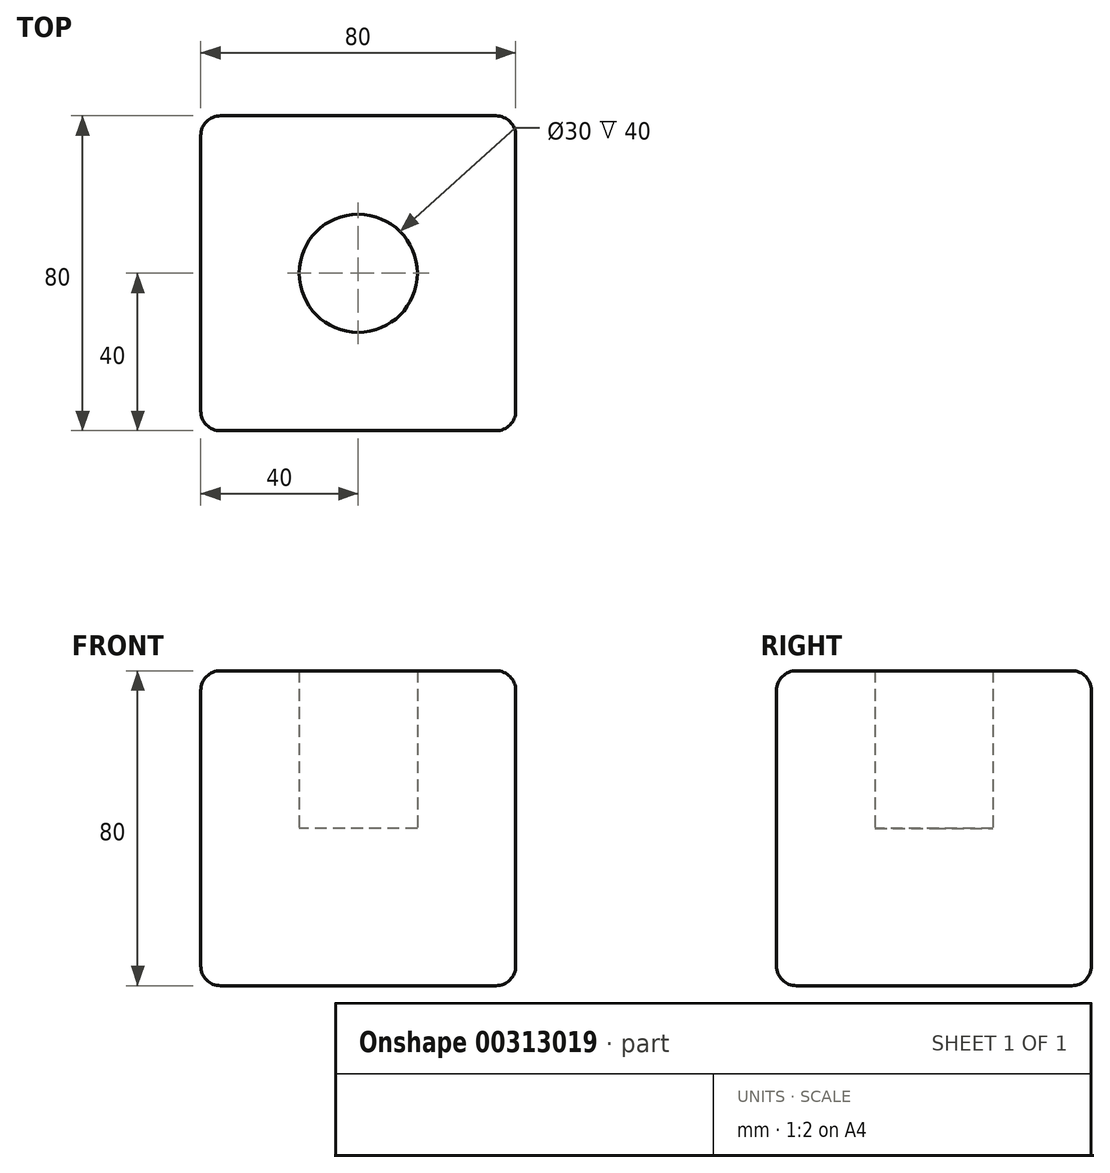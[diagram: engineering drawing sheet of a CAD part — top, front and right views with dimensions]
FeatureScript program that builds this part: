
annotation { "Feature Type Name" : "Feature", "Feature Type Description" : "" }
export const myFeature = defineFeature(function(context is Context, id is Id, definition is map)
    precondition{}
    {
        {
            var Q0;
            Q0=qCreatedBy(makeId("Top.planeOp"),FACE);
            var sketch = newSketch(context, id + "F0", { "sketchPlane" : qUnion([Q0])});
            skLineSegment(sketch, "E0.bottom", {"start": v(-40, 40) * mm, "end": v(40, 40) * mm});
            skLineSegment(sketch, "E0.top", {"start": v(-40, -40) * mm, "end": v(40, -40) * mm});
            skLineSegment(sketch, "E0.left", {"start": v(-40, 40) * mm, "end": v(-40, -40) * mm});
            skLineSegment(sketch, "E0.right", {"start": v(40, 40) * mm, "end": v(40, -40) * mm});
            skPoint(sketch, "E0.middle", {"position": v(0, 0) * mm});
            skSolve(sketch);
        }
        {
            var Q0;
            Q0=makeQuery(id+"F0.imprint","IMPRINT",FACE,{"disambiguationData":[TD([[makeQuery(id+"F0.imprint","IMPRINT",EDGE,{"derivedFrom":sQuery(id+"F0.wireOp",EDGE,"E0.bottom")}),-1.0]])]});
            extrude(context, id + "F1", {"entities" : qUnion([Q0]), "endBound" : BoundingType.SYMMETRIC, "depth" : 80 * mm});
        }
        {
            var Q0;
            Q0=makeQuery(id+"F1.opExtrude","CAP_EDGE",EDGE,{"disambiguationData":[OSD([sQuery(id+"F0.wireOp",EDGE,"E0.bottom")])],"isStart":false});
            var Q1;
            Q1=makeQuery(id+"F1.opExtrude","CAP_EDGE",EDGE,{"disambiguationData":[OSD([sQuery(id+"F0.wireOp",EDGE,"E0.left")])],"isStart":false});
            var Q2;
            Q2=makeQuery(id+"F1.opExtrude","CAP_EDGE",EDGE,{"disambiguationData":[OSD([sQuery(id+"F0.wireOp",EDGE,"E0.top")])],"isStart":false});
            var Q3;
            Q3=makeQuery(id+"F1.opExtrude","CAP_EDGE",EDGE,{"disambiguationData":[OSD([sQuery(id+"F0.wireOp",EDGE,"E0.right")])],"isStart":false});
            var Q4;
            Q4=makeQuery(id+"F1.opExtrude","SWEPT_EDGE",EDGE,{"disambiguationData":[OSD([sQuery(id+"F0.wireOp",EDGE,"E0.top"),sQuery(id+"F0.wireOp",EDGE,"E0.right")])]});
            var Q5;
            Q5=makeQuery(id+"F1.opExtrude","SWEPT_EDGE",EDGE,{"disambiguationData":[OSD([sQuery(id+"F0.wireOp",EDGE,"E0.bottom"),sQuery(id+"F0.wireOp",EDGE,"E0.right")])]});
            var Q6;
            Q6=makeQuery(id+"F1.opExtrude","CAP_EDGE",EDGE,{"disambiguationData":[OSD([sQuery(id+"F0.wireOp",EDGE,"E0.right")])],"isStart":true});
            var Q7;
            Q7=makeQuery(id+"F1.opExtrude","CAP_EDGE",EDGE,{"disambiguationData":[OSD([sQuery(id+"F0.wireOp",EDGE,"E0.top")])],"isStart":true});
            var Q8;
            Q8=makeQuery(id+"F1.opExtrude","SWEPT_EDGE",EDGE,{"disambiguationData":[OSD([sQuery(id+"F0.wireOp",EDGE,"E0.top"),sQuery(id+"F0.wireOp",EDGE,"E0.left")])]});
            var Q9;
            Q9=makeQuery(id+"F1.opExtrude","CAP_EDGE",EDGE,{"disambiguationData":[OSD([sQuery(id+"F0.wireOp",EDGE,"E0.left")])],"isStart":true});
            var Q10;
            Q10=makeQuery(id+"F1.opExtrude","CAP_EDGE",EDGE,{"disambiguationData":[OSD([sQuery(id+"F0.wireOp",EDGE,"E0.bottom")])],"isStart":true});
            var Q11;
            Q11=makeQuery(id+"F1.opExtrude","SWEPT_EDGE",EDGE,{"disambiguationData":[OSD([sQuery(id+"F0.wireOp",EDGE,"E0.bottom"),sQuery(id+"F0.wireOp",EDGE,"E0.left")])]});
            fillet(context, id + "F2", {"entities" : qUnion([Q0, Q1, Q2, Q3, Q4, Q5, Q6, Q7, Q8, Q9, Q10, Q11]), "radius" : 5 * mm, "tangentPropagation" : true, "allowEdgeOverflow" : false});
        }
        {
            var Q0;
            Q0=qCreatedBy(makeId("Top.planeOp"),FACE);
            var sketch = newSketch(context, id + "F3", { "sketchPlane" : qUnion([Q0])});
            skCircle(sketch, "E1", {"center": v(0, 0) * mm, "radius": 15 * mm});
            skSolve(sketch);
        }
        {
            var Q0;
            Q0 = qSketchRegion(id + "F3", true);
            extrude(context, id + "F4", {"entities" : qUnion([Q0]), "operationType" : NewBodyOperationType.REMOVE, "endBound" : BoundingType.THROUGH_ALL, "depth" : 25 * mm});
        }
    });
